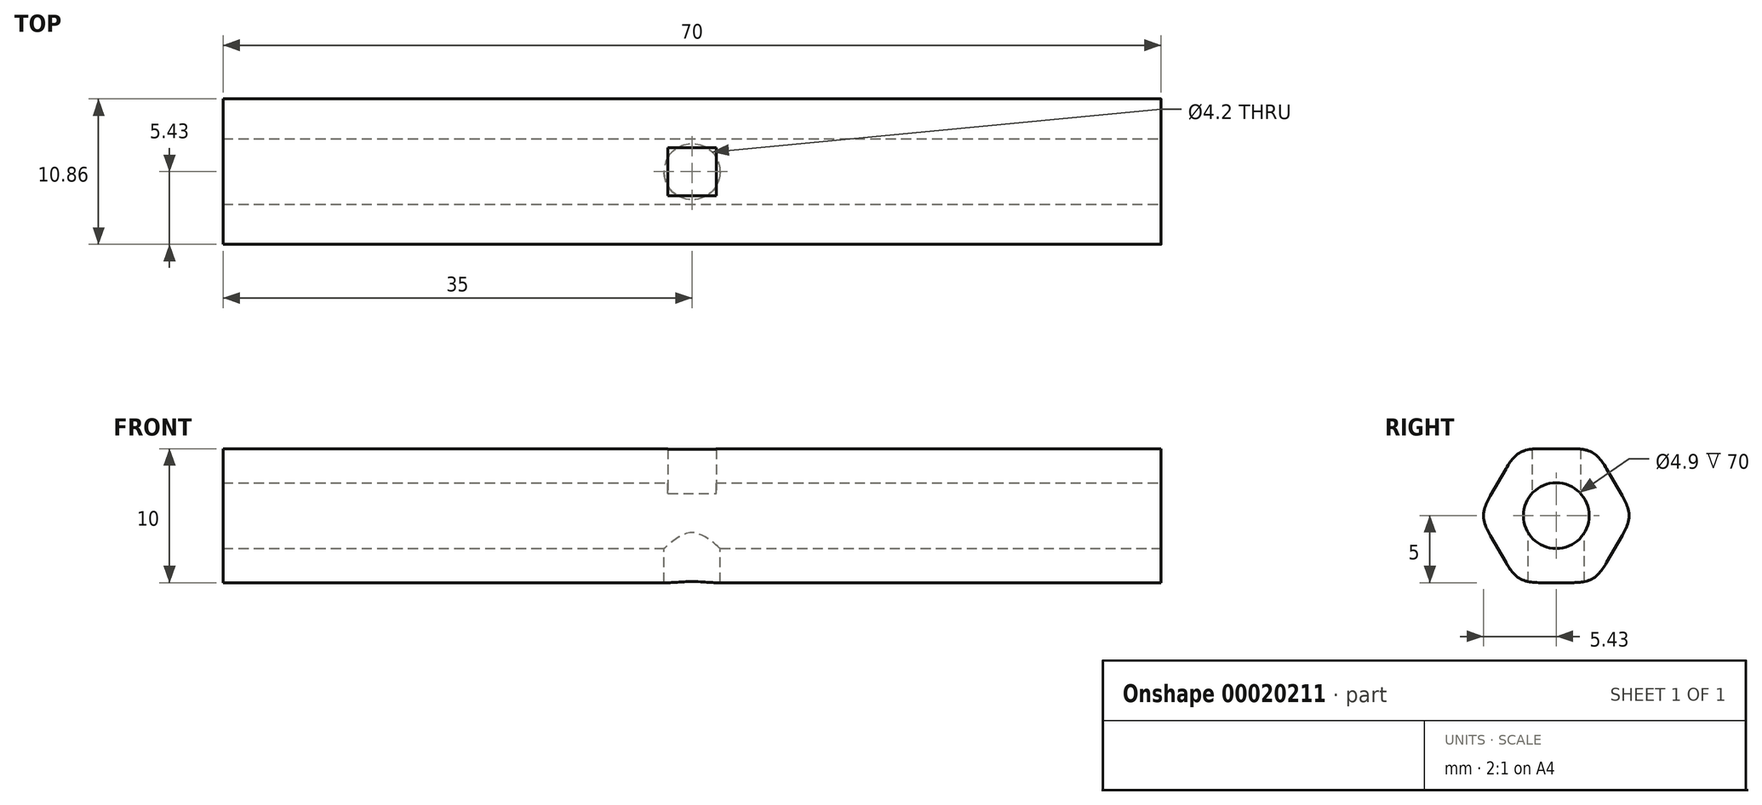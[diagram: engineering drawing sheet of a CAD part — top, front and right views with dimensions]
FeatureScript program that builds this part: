
annotation { "Feature Type Name" : "Feature", "Feature Type Description" : "" }
export const myFeature = defineFeature(function(context is Context, id is Id, definition is map)
    precondition{}
    {
        {
            var Q0;
            Q0=qCreatedBy(makeId("Right.planeOp"),FACE);
            var sketch = newSketch(context, id + "F0", { "sketchPlane" : qUnion([Q0])});
            skCircle(sketch, "E0", {"center": v(0, 0) * mm, "radius": 5 * mm, "construction": true});
            skLineSegment(sketch, "E1", {"start": v(-2.89, 5) * mm, "end": v(2.89, 5) * mm});
            skLineSegment(sketch, "E2", {"start": v(2.89, 5) * mm, "end": v(5.77, 0) * mm});
            skLineSegment(sketch, "E3", {"start": v(5.77, 0) * mm, "end": v(2.89, -5) * mm});
            skLineSegment(sketch, "E4", {"start": v(2.89, -5) * mm, "end": v(-2.89, -5) * mm});
            skLineSegment(sketch, "E5", {"start": v(-2.89, -5) * mm, "end": v(-5.77, 0) * mm});
            skLineSegment(sketch, "E6", {"start": v(-5.77, 0) * mm, "end": v(-2.89, 5) * mm});
            skSolve(sketch);
        }
        {
            var Q0;
            Q0=makeQuery(id+"F0.imprint","IMPRINT",FACE,{"disambiguationData":[TD([[makeQuery(id+"F0.imprint","IMPRINT",EDGE,{"derivedFrom":sQuery(id+"F0.wireOp",EDGE,"E1")}),-1.0]])]});
            extrude(context, id + "F1", {"entities" : qUnion([Q0]), "endBound" : BoundingType.SYMMETRIC, "depth" : 70 * mm});
        }
        {
            var Q0;
            Q0=makeQuery(id+"F1.opExtrude","CAP_FACE",FACE,{"disambiguationData":[OSD([sQuery(id+"F0.wireOp",EDGE,"E1"),sQuery(id+"F0.wireOp",EDGE,"E2"),sQuery(id+"F0.wireOp",EDGE,"E3"),sQuery(id+"F0.wireOp",EDGE,"E4"),sQuery(id+"F0.wireOp",EDGE,"E5"),sQuery(id+"F0.wireOp",EDGE,"E6")])],"isStart":false});
            var sketch = newSketch(context, id + "F2", { "sketchPlane" : qUnion([Q0])});
            skCircle(sketch, "E7", {"center": v(0, 0) * mm, "radius": 2.45 * mm});
            skSolve(sketch);
        }
        {
            var Q0;
            Q0=qSketchRegion(id+"F2",true);
            extrude(context, id + "F3", {"entities" : qUnion([Q0]), "operationType" : NewBodyOperationType.REMOVE, "endBound" : BoundingType.THROUGH_ALL, "oppositeDirection" : true, "depth" : 25 * mm});
        }
        {
            var Q0;
            Q0=qCreatedBy(makeId("Top.planeOp"),FACE);
            var sketch = newSketch(context, id + "F4", { "sketchPlane" : qUnion([Q0])});
            skLineSegment(sketch, "E8.rect.bottom", {"start": v(-1.8, 1.8) * mm, "end": v(1.8, 1.8) * mm});
            skLineSegment(sketch, "E8.rect.top", {"start": v(-1.8, -1.8) * mm, "end": v(1.8, -1.8) * mm});
            skLineSegment(sketch, "E8.rect.left", {"start": v(-1.8, 1.8) * mm, "end": v(-1.8, -1.8) * mm});
            skLineSegment(sketch, "E8.rect.right", {"start": v(1.8, 1.8) * mm, "end": v(1.8, -1.8) * mm});
            skPoint(sketch, "E8.rect.middle", {"position": v(0, 0) * mm});
            skSolve(sketch);
        }
        {
            var Q0;
            Q0=qSketchRegion(id+"F4",true);
            var Q1;
            Q1=makeQuery(id+"F1.opExtrude","SWEPT_FACE",FACE,{"disambiguationData":[OSD([sQuery(id+"F0.wireOp",EDGE,"E1")])]});
            extrude(context, id + "F5", {"entities" : qUnion([Q0]), "operationType" : NewBodyOperationType.REMOVE, "endBound" : BoundingType.THROUGH_ALL, "endBoundEntityFace" : qUnion([Q1]), "depth" : 12 * mm});
        }
        {
            var Q0;
            Q0=makeQuery(id+"F1.opExtrude","SWEPT_EDGE",EDGE,{"disambiguationData":[OSD([sQuery(id+"F0.wireOp",EDGE,"E1"),sQuery(id+"F0.wireOp",EDGE,"E6")])]});
            var Q1;
            Q1=makeQuery(id+"F1.opExtrude","SWEPT_EDGE",EDGE,{"disambiguationData":[OSD([sQuery(id+"F0.wireOp",EDGE,"E1"),sQuery(id+"F0.wireOp",EDGE,"E2")])]});
            var Q2;
            Q2=makeQuery(id+"F1.opExtrude","SWEPT_EDGE",EDGE,{"disambiguationData":[OSD([sQuery(id+"F0.wireOp",EDGE,"E2"),sQuery(id+"F0.wireOp",EDGE,"E3")])]});
            var Q3;
            Q3=makeQuery(id+"F1.opExtrude","SWEPT_EDGE",EDGE,{"disambiguationData":[OSD([sQuery(id+"F0.wireOp",EDGE,"E5"),sQuery(id+"F0.wireOp",EDGE,"E6")])]});
            var Q4;
            Q4=makeQuery(id+"F1.opExtrude","SWEPT_EDGE",EDGE,{"disambiguationData":[OSD([sQuery(id+"F0.wireOp",EDGE,"E3"),sQuery(id+"F0.wireOp",EDGE,"E4")])]});
            var Q5;
            Q5=makeQuery(id+"F1.opExtrude","SWEPT_EDGE",EDGE,{"disambiguationData":[OSD([sQuery(id+"F0.wireOp",EDGE,"E4"),sQuery(id+"F0.wireOp",EDGE,"E5")])]});
            fillet(context, id + "F6", {"entities" : qUnion([Q0, Q1, Q2, Q3, Q4, Q5]), "radius" : 3 * mm, "tangentPropagation" : true, "rho" : .6, "crossSection" : FilletCrossSection.CONIC, "allowEdgeOverflow" : false});
        }
        {
            var Q0;
            Q0=qCreatedBy(makeId("Top.planeOp"),FACE);
            var sketch = newSketch(context, id + "F7", { "sketchPlane" : qUnion([Q0])});
            skCircle(sketch, "E9", {"center": v(0, 0) * mm, "radius": 2.1 * mm});
            skSolve(sketch);
        }
        {
            var Q0;
            Q0=qSketchRegion(id+"F7",true);
            extrude(context, id + "F8", {"entities" : qUnion([Q0]), "operationType" : NewBodyOperationType.REMOVE, "endBound" : BoundingType.THROUGH_ALL, "oppositeDirection" : true, "depth" : 25 * mm});
        }
    });
